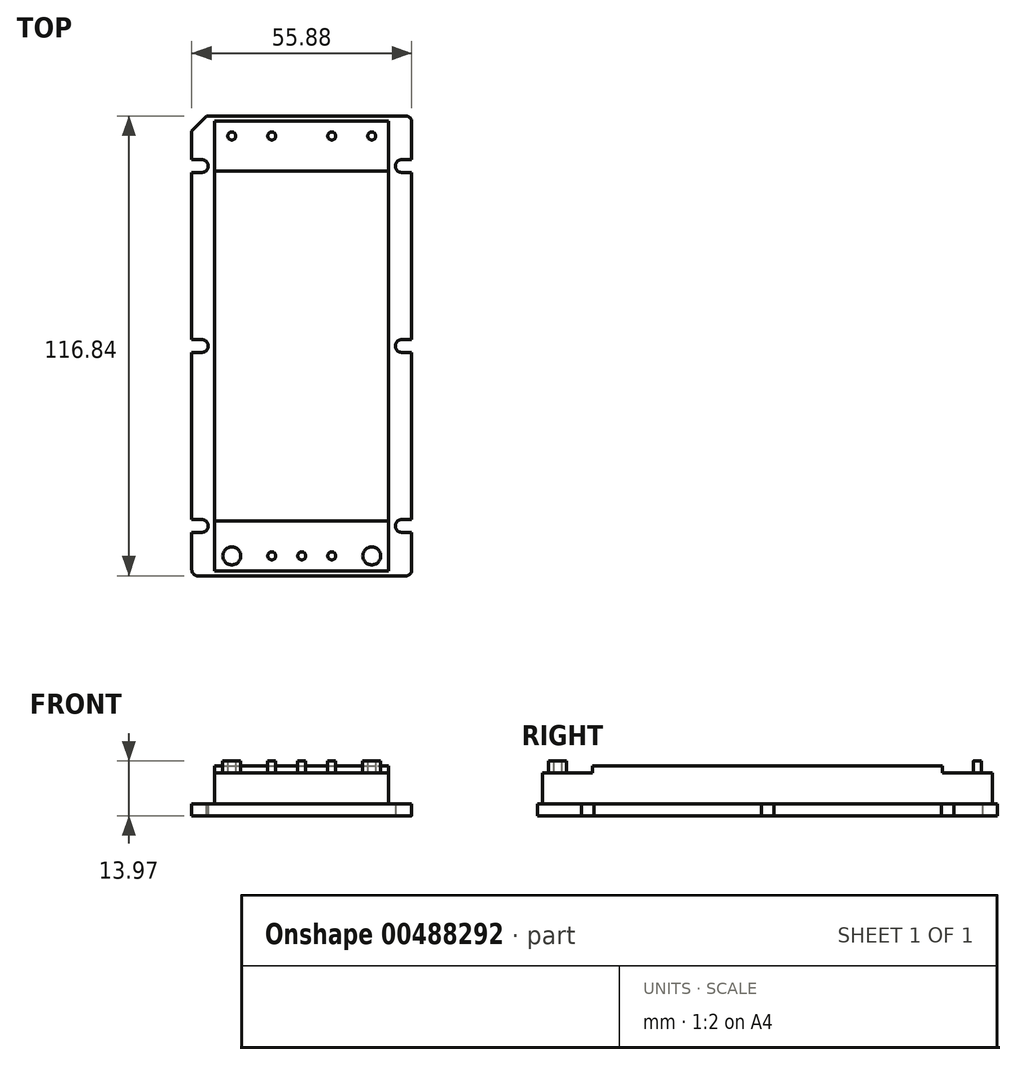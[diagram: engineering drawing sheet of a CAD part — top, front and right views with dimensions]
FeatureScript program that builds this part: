
annotation { "Feature Type Name" : "Feature", "Feature Type Description" : "" }
export const myFeature = defineFeature(function(context is Context, id is Id, definition is map)
    precondition{}
    {
        {
            var Q0;
            Q0=qCreatedBy(makeId("Top.planeOp"),FACE);
            var sketch = newSketch(context, id + "F0", { "sketchPlane" : qUnion([Q0])});
            skLineSegment(sketch, "E0.bottom", {"start": v(27.94, -58.42) * mm, "end": v(-27.94, -58.42) * mm});
            skLineSegment(sketch, "E0.top", {"start": v(27.94, 58.42) * mm, "end": v(-27.94, 58.42) * mm});
            skLineSegment(sketch, "E0.left", {"start": v(27.94, -58.42) * mm, "end": v(27.94, 58.42) * mm});
            skLineSegment(sketch, "E0.right", {"start": v(-27.94, -58.42) * mm, "end": v(-27.94, 58.42) * mm});
            skPoint(sketch, "E0.middle", {"position": v(0, 0) * mm});
            skCircle(sketch, "E1", {"center": v(-25.4, 45.72) * mm, "radius": 1.64 * mm});
            skCircle(sketch, "E2", {"center": v(-25.4, 0) * mm, "radius": 1.64 * mm});
            skLineSegment(sketch, "E3", {"start": v(-25.4, 47.36) * mm, "end": v(-27.94, 47.36) * mm});
            skLineSegment(sketch, "E4", {"start": v(-25.4, 44.08) * mm, "end": v(-27.94, 44.08) * mm});
            skLineSegment(sketch, "E5", {"start": v(-25.4, -1.64) * mm, "end": v(-27.94, -1.64) * mm});
            skLineSegment(sketch, "E6", {"start": v(-25.4, 1.64) * mm, "end": v(-27.94, 1.64) * mm});
            skLineSegment(sketch, "E7.MirrorCS", {"start": v(25.4, 44.08) * mm, "end": v(27.94, 44.08) * mm});
            skCircle(sketch, "E8.MirrorC", {"center": v(25.4, 45.72) * mm, "radius": 1.64 * mm});
            skLineSegment(sketch, "E9.MirrorCS", {"start": v(25.4, 47.36) * mm, "end": v(27.94, 47.36) * mm});
            skLineSegment(sketch, "E10.MirrorCS", {"start": v(25.4, -1.64) * mm, "end": v(27.94, -1.64) * mm});
            skCircle(sketch, "E11.MirrorC", {"center": v(25.4, 0) * mm, "radius": 1.64 * mm});
            skLineSegment(sketch, "E12.MirrorCS", {"start": v(25.4, 1.64) * mm, "end": v(27.94, 1.64) * mm});
            skLineSegment(sketch, "E13.MirrorCS", {"start": v(-25.4, -44.08) * mm, "end": v(-27.94, -44.08) * mm});
            skCircle(sketch, "E14.MirrorC", {"center": v(-25.4, -45.72) * mm, "radius": 1.64 * mm});
            skLineSegment(sketch, "E15.MirrorCS", {"start": v(-25.4, -47.36) * mm, "end": v(-27.94, -47.36) * mm});
            skCircle(sketch, "E16.MirrorC", {"center": v(25.4, -45.72) * mm, "radius": 1.64 * mm});
            skLineSegment(sketch, "E17.MirrorCS", {"start": v(25.4, -44.08) * mm, "end": v(27.94, -44.08) * mm});
            skLineSegment(sketch, "E18.MirrorCS", {"start": v(25.4, -47.36) * mm, "end": v(27.94, -47.36) * mm});
            skSolve(sketch);
        }
        {
            var Q0;
            {var subQ16=sQuery(id+"F0.wireOp",EDGE,"E0.bottom");Q0=makeQuery(id+"F0.imprint","IMPRINT",FACE,{"disambiguationData":[TD([[makeQuery(id+"F0.imprint","IMPRINT",EDGE,{"derivedFrom":subQ16}),-1.0]])]});}
            extrude(context, id + "F1", {"entities" : qUnion([Q0]), "depth" : 3.05 * mm});
        }
        {
            var Q0;
            Q0=makeQuery(id+"F1.opExtrude","SWEPT_EDGE",EDGE,{"disambiguationData":[OSD([sQuery(id+"F0.wireOp",EDGE,"E0.top"),sQuery(id+"F0.wireOp",EDGE,"E0.right")])]});
            chamfer(context, id + "F2", {"entities" : qUnion([Q0]), "width" : 3.8 * mm, "tangentPropagation" : true});
        }
        {
            var Q0;
            Q0=makeQuery(id+"F1.opExtrude","SWEPT_EDGE",EDGE,{"disambiguationData":[OSD([sQuery(id+"F0.wireOp",EDGE,"E0.top"),sQuery(id+"F0.wireOp",EDGE,"E0.left")])]});
            var Q1;
            Q1=makeQuery(id+"F1.opExtrude","SWEPT_EDGE",EDGE,{"disambiguationData":[OSD([sQuery(id+"F0.wireOp",EDGE,"E0.bottom"),sQuery(id+"F0.wireOp",EDGE,"E0.left")])]});
            var Q2;
            Q2=makeQuery(id+"F1.opExtrude","SWEPT_EDGE",EDGE,{"disambiguationData":[OSD([sQuery(id+"F0.wireOp",EDGE,"E0.bottom"),sQuery(id+"F0.wireOp",EDGE,"E0.right")])]});
            fillet(context, id + "F3", {"entities" : qUnion([Q0, Q1, Q2]), "radius" : 1.52 * mm, "tangentPropagation" : true, "allowEdgeOverflow" : false});
        }
        {
            var Q0;
            Q0=makeQuery(id+"F1.opExtrude","CAP_FACE",FACE,{"disambiguationData":[OSD([sQuery(id+"F0.wireOp",EDGE,"E0.bottom"),sQuery(id+"F0.wireOp",EDGE,"E0.top"),sQuery(id+"F0.wireOp",EDGE,"E0.left"),sQuery(id+"F0.wireOp",EDGE,"E0.right"),sQuery(id+"F0.wireOp",EDGE,"E1"),sQuery(id+"F0.wireOp",EDGE,"E2"),sQuery(id+"F0.wireOp",EDGE,"E3"),sQuery(id+"F0.wireOp",EDGE,"E4"),sQuery(id+"F0.wireOp",EDGE,"E5"),sQuery(id+"F0.wireOp",EDGE,"E6"),sQuery(id+"F0.wireOp",EDGE,"E7.MirrorCS"),sQuery(id+"F0.wireOp",EDGE,"E8.MirrorC"),sQuery(id+"F0.wireOp",EDGE,"E9.MirrorCS"),sQuery(id+"F0.wireOp",EDGE,"E10.MirrorCS"),sQuery(id+"F0.wireOp",EDGE,"E11.MirrorC"),sQuery(id+"F0.wireOp",EDGE,"E12.MirrorCS"),sQuery(id+"F0.wireOp",EDGE,"E13.MirrorCS"),sQuery(id+"F0.wireOp",EDGE,"E14.MirrorC"),sQuery(id+"F0.wireOp",EDGE,"E15.MirrorCS"),sQuery(id+"F0.wireOp",EDGE,"E16.MirrorC"),sQuery(id+"F0.wireOp",EDGE,"E17.MirrorCS"),sQuery(id+"F0.wireOp",EDGE,"E18.MirrorCS")])],"isStart":false});
            var sketch = newSketch(context, id + "F4", { "sketchPlane" : qUnion([Q0])});
            skLineSegment(sketch, "E19.bottom", {"start": v(22.1, -57.15) * mm, "end": v(-22.1, -57.15) * mm});
            skLineSegment(sketch, "E19.top", {"start": v(22.1, 57.15) * mm, "end": v(-22.1, 57.15) * mm});
            skLineSegment(sketch, "E19.left", {"start": v(22.1, -57.15) * mm, "end": v(22.1, 57.15) * mm});
            skLineSegment(sketch, "E19.right", {"start": v(-22.1, -57.15) * mm, "end": v(-22.1, 57.15) * mm});
            skPoint(sketch, "E19.middle", {"position": v(0, 0) * mm});
            skSolve(sketch);
        }
        {
            var Q0;
            Q0 = qSketchRegion(id + "F4", true);
            extrude(context, id + "F5", {"entities" : qUnion([Q0]), "operationType" : NewBodyOperationType.ADD, "depth" : 9.65 * mm});
        }
        {
            var Q0;
            Q0=makeQuery(id+"F5.opExtrude","CAP_FACE",FACE,{"disambiguationData":[OSD([sQuery(id+"F4.wireOp",EDGE,"E19.bottom"),sQuery(id+"F4.wireOp",EDGE,"E19.top"),sQuery(id+"F4.wireOp",EDGE,"E19.left"),sQuery(id+"F4.wireOp",EDGE,"E19.right")])],"isStart":false});
            var sketch = newSketch(context, id + "F6", { "sketchPlane" : qUnion([Q0])});
            skLineSegment(sketch, "E20.bottom", {"start": v(-22.1, -57.15) * mm, "end": v(22.1, -57.15) * mm});
            skLineSegment(sketch, "E20.top", {"start": v(-22.1, -44.45) * mm, "end": v(22.1, -44.45) * mm});
            skLineSegment(sketch, "E20.left", {"start": v(-22.1, -57.15) * mm, "end": v(-22.1, -44.45) * mm});
            skLineSegment(sketch, "E20.right", {"start": v(22.1, -57.15) * mm, "end": v(22.1, -44.45) * mm});
            skLineSegment(sketch, "E21.bottom", {"start": v(-22.1, 57.15) * mm, "end": v(22.1, 57.15) * mm});
            skLineSegment(sketch, "E21.top", {"start": v(-22.1, 44.45) * mm, "end": v(22.1, 44.45) * mm});
            skLineSegment(sketch, "E21.left", {"start": v(-22.1, 57.15) * mm, "end": v(-22.1, 44.45) * mm});
            skLineSegment(sketch, "E21.right", {"start": v(22.1, 57.15) * mm, "end": v(22.1, 44.45) * mm});
            skSolve(sketch);
        }
        {
            var Q0;
            Q0 = qSketchRegion(id + "F6", true);
            extrude(context, id + "F7", {"entities" : qUnion([Q0]), "operationType" : NewBodyOperationType.REMOVE, "oppositeDirection" : true, "depth" : 1.78 * mm});
        }
        {
            var Q0;
            Q0=makeQuery(id+"F7.boolean.opBoolean","COPY",FACE,{"derivedFrom":makeQuery(id+"F7.opExtrude","CAP_FACE",FACE,{"disambiguationData":[OSD([sQuery(id+"F6.wireOp",EDGE,"E20.bottom"),sQuery(id+"F6.wireOp",EDGE,"E20.top"),sQuery(id+"F6.wireOp",EDGE,"E20.left"),sQuery(id+"F6.wireOp",EDGE,"E20.right")])],"isStart":false})});
            var sketch = newSketch(context, id + "F8", { "sketchPlane" : qUnion([Q0])});
            skCircle(sketch, "E22", {"center": v(-17.78, -53.34) * mm, "radius": 2.29 * mm});
            skCircle(sketch, "E23", {"center": v(17.78, -53.34) * mm, "radius": 2.29 * mm});
            skSolve(sketch);
        }
        {
            var Q0;
            Q0 = qSketchRegion(id + "F8", true);
            extrude(context, id + "F9", {"entities" : qUnion([Q0]), "operationType" : NewBodyOperationType.ADD, "depth" : 3.05 * mm});
        }
        {
            var Q0;
            Q0=makeQuery(id+"F7.boolean.opBoolean","COPY",FACE,{"derivedFrom":makeQuery(id+"F7.opExtrude","CAP_FACE",FACE,{"disambiguationData":[OSD([sQuery(id+"F6.wireOp",EDGE,"E20.bottom"),sQuery(id+"F6.wireOp",EDGE,"E20.top"),sQuery(id+"F6.wireOp",EDGE,"E20.left"),sQuery(id+"F6.wireOp",EDGE,"E20.right")])],"isStart":false})});
            var sketch = newSketch(context, id + "F10", { "sketchPlane" : qUnion([Q0])});
            skCircle(sketch, "E24", {"center": v(0, -53.34) * mm, "radius": 1.02 * mm});
            skCircle(sketch, "E25", {"center": v(7.62, -53.34) * mm, "radius": 1.02 * mm});
            skCircle(sketch, "E26", {"center": v(-7.62, -53.34) * mm, "radius": 1.02 * mm});
            skCircle(sketch, "E27", {"center": v(-7.62, 53.34) * mm, "radius": 1.02 * mm});
            skCircle(sketch, "E28", {"center": v(-17.78, 53.34) * mm, "radius": 1.02 * mm});
            skCircle(sketch, "E29", {"center": v(7.62, 53.34) * mm, "radius": 1.02 * mm});
            skCircle(sketch, "E30", {"center": v(17.78, 53.34) * mm, "radius": 1.02 * mm});
            skCircle(sketch, "E31.0.0", {"center": v(-17.78, -53.34) * mm, "radius": 2.29 * mm});
            skCircle(sketch, "E31.1.0", {"center": v(17.78, -53.34) * mm, "radius": 2.29 * mm});
            skSolve(sketch);
        }
        {
            var Q0;
            Q0=makeQuery(id+"F10.imprint","IMPRINT",FACE,{"disambiguationData":[TD([[makeQuery(id+"F10.imprint","IMPRINT",EDGE,{"derivedFrom":sQuery(id+"F10.wireOp",EDGE,"E26")}),1.0]])]});
            var Q1;
            Q1=makeQuery(id+"F10.imprint","IMPRINT",FACE,{"disambiguationData":[TD([[makeQuery(id+"F10.imprint","IMPRINT",EDGE,{"derivedFrom":sQuery(id+"F10.wireOp",EDGE,"E24")}),1.0]])]});
            var Q2;
            Q2=makeQuery(id+"F10.imprint","IMPRINT",FACE,{"disambiguationData":[TD([[makeQuery(id+"F10.imprint","IMPRINT",EDGE,{"derivedFrom":sQuery(id+"F10.wireOp",EDGE,"E25")}),1.0]])]});
            var Q3;
            Q3=makeQuery(id+"F10.imprint","IMPRINT",FACE,{"disambiguationData":[TD([[makeQuery(id+"F10.imprint","IMPRINT",EDGE,{"derivedFrom":sQuery(id+"F10.wireOp",EDGE,"E28")}),1.0]])]});
            var Q4;
            Q4=makeQuery(id+"F10.imprint","IMPRINT",FACE,{"disambiguationData":[TD([[makeQuery(id+"F10.imprint","IMPRINT",EDGE,{"derivedFrom":sQuery(id+"F10.wireOp",EDGE,"E27")}),1.0]])]});
            var Q5;
            Q5=makeQuery(id+"F10.imprint","IMPRINT",FACE,{"disambiguationData":[TD([[makeQuery(id+"F10.imprint","IMPRINT",EDGE,{"derivedFrom":sQuery(id+"F10.wireOp",EDGE,"E29")}),1.0]])]});
            var Q6;
            Q6=makeQuery(id+"F10.imprint","IMPRINT",FACE,{"disambiguationData":[TD([[makeQuery(id+"F10.imprint","IMPRINT",EDGE,{"derivedFrom":sQuery(id+"F10.wireOp",EDGE,"E30")}),1.0]])]});
            var Q7;
            Q7=makeQuery(id+"F9.opExtrude","CAP_FACE",FACE,{"disambiguationData":[OSD([sQuery(id+"F8.wireOp",EDGE,"E23")])],"isStart":false});
            extrude(context, id + "F11", {"entities" : qUnion([Q0, Q1, Q2, Q3, Q4, Q5, Q6]), "operationType" : NewBodyOperationType.ADD, "endBound" : BoundingType.UP_TO_SURFACE, "endBoundEntityFace" : qUnion([Q7]), "depth" : 25.4 * mm});
        }
    });
